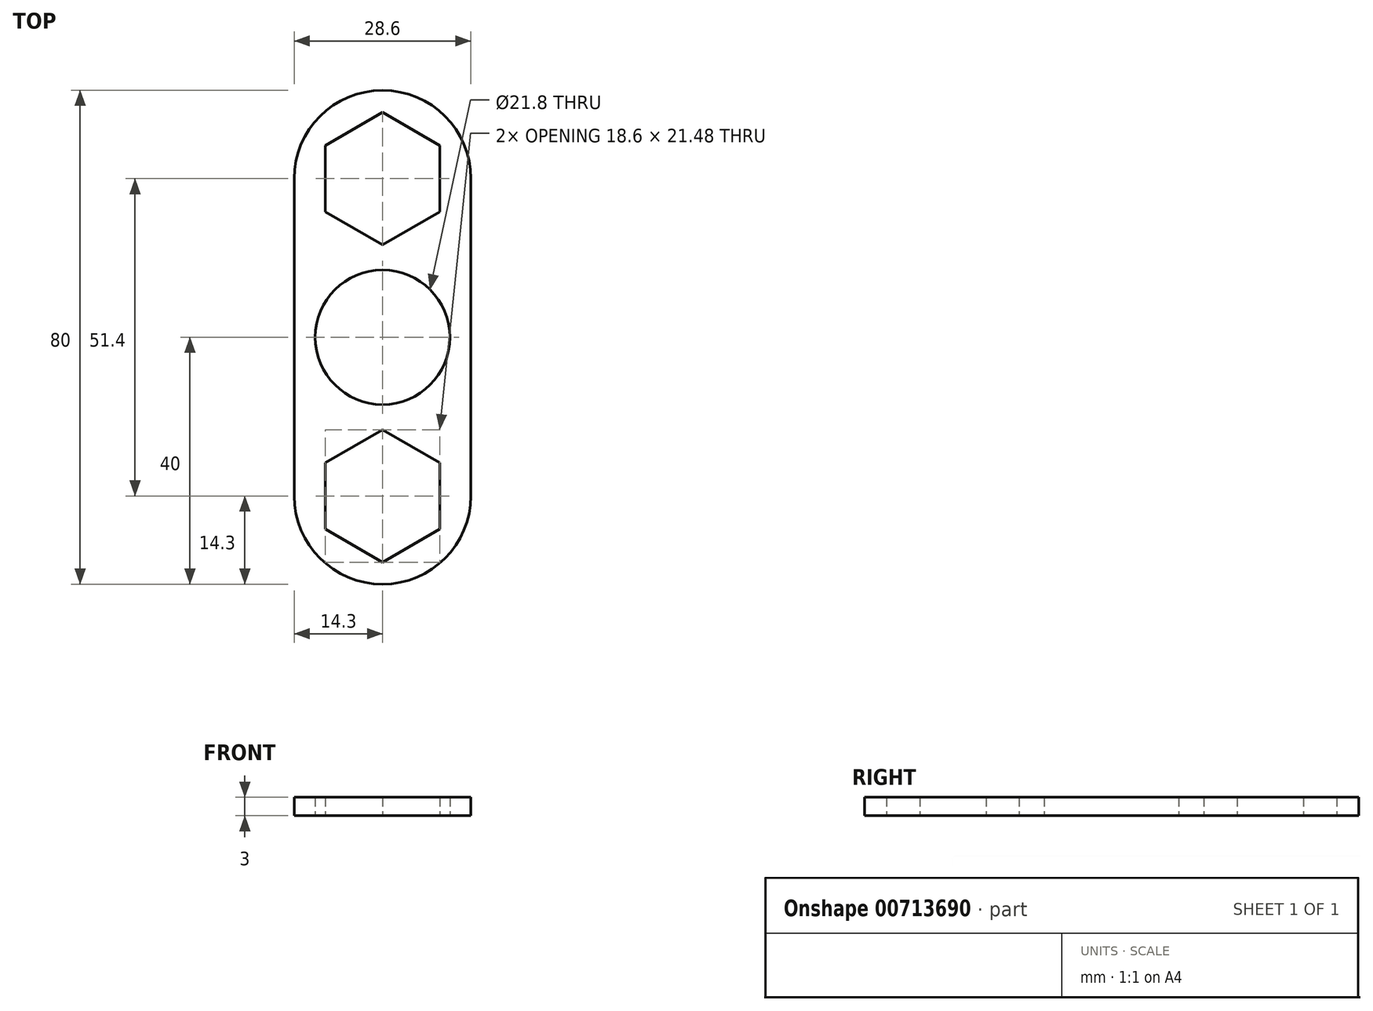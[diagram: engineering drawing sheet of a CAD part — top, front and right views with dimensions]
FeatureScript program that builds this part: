
annotation { "Feature Type Name" : "Feature", "Feature Type Description" : "" }
export const myFeature = defineFeature(function(context is Context, id is Id, definition is map)
    precondition{}
    {
        {
            var Q0;
            Q0=qCreatedBy(makeId("Top.planeOp"),FACE);
            var sketch = newSketch(context, id + "F0", { "sketchPlane" : qUnion([Q0])});
            skCircle(sketch, "E0", {"center": v(0, 0) * mm, "radius": 10.9 * mm});
            skCircle(sketch, "E1.cCircle", {"center": v(0, 25.7) * mm, "radius": 9.3 * mm, "construction": true});
            skLineSegment(sketch, "E1.0", {"start": v(-9.3, 20.33) * mm, "end": v(-9.3, 31.07) * mm});
            skLineSegment(sketch, "E1.1", {"start": v(-9.3, 31.07) * mm, "end": v(0, 36.44) * mm});
            skLineSegment(sketch, "E1.2", {"start": v(0, 36.44) * mm, "end": v(9.3, 31.07) * mm});
            skLineSegment(sketch, "E1.3", {"start": v(9.3, 31.07) * mm, "end": v(9.3, 20.33) * mm});
            skLineSegment(sketch, "E1.4", {"start": v(9.3, 20.33) * mm, "end": v(0, 14.96) * mm});
            skLineSegment(sketch, "E1.5", {"start": v(0, 14.96) * mm, "end": v(-9.3, 20.33) * mm});
            skPoint(sketch, "E1.0.midPoint", {"position": v(-9.3, 25.7) * mm});
            skArc(sketch, "E2", {"start": v(14.3, 25.7) * mm, "mid": v(0, 40) * mm, "end": v(-14.3, 25.7) * mm});
            skLineSegment(sketch, "E3", {"start": v(-14.3, 25.7) * mm, "end": v(-14.3, 0) * mm});
            skLineSegment(sketch, "E4", {"start": v(0, 0) * mm, "end": v(0, 45.21) * mm, "construction": true});
            skLineSegment(sketch, "E5", {"start": v(0, 0) * mm, "end": v(-23.12, 0) * mm, "construction": true});
            skLineSegment(sketch, "E6.MirrorCS", {"start": v(14.3, 25.7) * mm, "end": v(14.3, 0) * mm});
            skLineSegment(sketch, "E7.MirrorCS", {"start": v(-14.3, -25.7) * mm, "end": v(-14.3, 0) * mm});
            skArc(sketch, "E8.MirrorCS", {"start": v(14.3, -25.7) * mm, "mid": v(0, -40) * mm, "end": v(-14.3, -25.7) * mm});
            skLineSegment(sketch, "E9.MirrorCS", {"start": v(14.3, -25.7) * mm, "end": v(14.3, 0) * mm});
            skLineSegment(sketch, "E10.MirrorCS", {"start": v(9.3, -20.33) * mm, "end": v(0, -14.96) * mm});
            skLineSegment(sketch, "E11.MirrorCS", {"start": v(0, -14.96) * mm, "end": v(-9.3, -20.33) * mm});
            skLineSegment(sketch, "E12.MirrorCS", {"start": v(-9.3, -20.33) * mm, "end": v(-9.3, -31.07) * mm});
            skLineSegment(sketch, "E13.MirrorCS", {"start": v(-9.3, -31.07) * mm, "end": v(0, -36.44) * mm});
            skLineSegment(sketch, "E14.MirrorCS", {"start": v(0, -36.44) * mm, "end": v(9.3, -31.07) * mm});
            skLineSegment(sketch, "E15.MirrorCS", {"start": v(9.3, -31.07) * mm, "end": v(9.3, -20.33) * mm});
            skSolve(sketch);
        }
        {
            var Q0;
            Q0=qSketchRegion(id+"F0",true);
            extrude(context, id + "F1", {"entities" : qUnion([Q0]), "depth" : 3 * mm, "offsetDistance" : 25 * mm});
        }
    });
